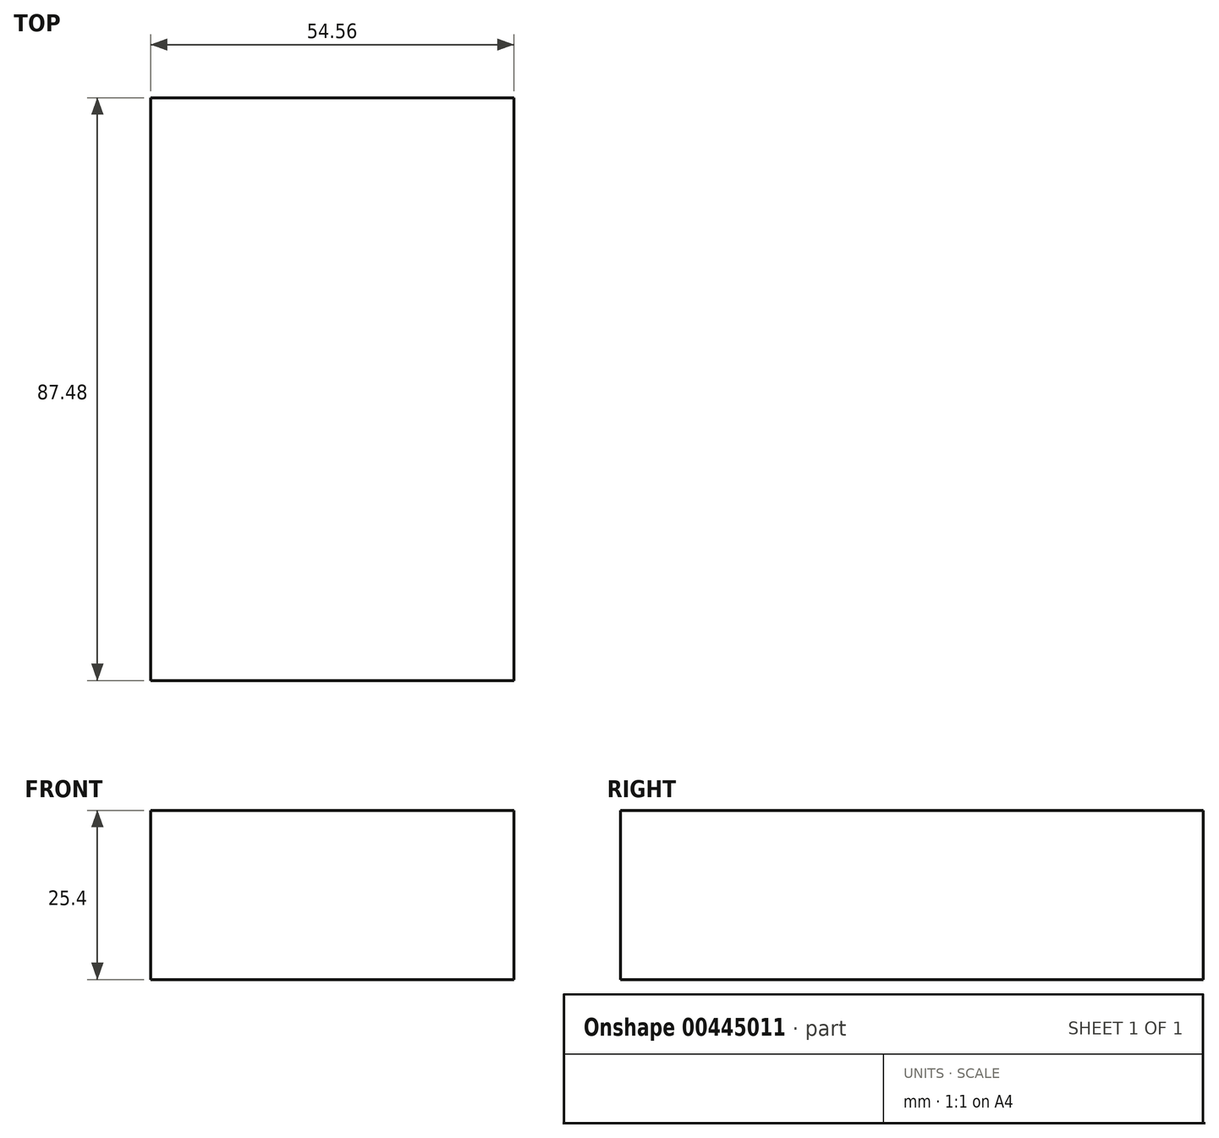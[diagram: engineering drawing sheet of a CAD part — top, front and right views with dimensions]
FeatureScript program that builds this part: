
annotation { "Feature Type Name" : "Feature", "Feature Type Description" : "" }
export const myFeature = defineFeature(function(context is Context, id is Id, definition is map)
    precondition{}
    {
        {
            var Q0;
            Q0=qCreatedBy(makeId("Top.planeOp"),FACE);
            var sketch = newSketch(context, id + "F0", { "sketchPlane" : qUnion([Q0])});
            skLineSegment(sketch, "E0.bottom", {"start": v(-23.9, -42.62) * mm, "end": v(30.65, -42.62) * mm});
            skLineSegment(sketch, "E0.top", {"start": v(-23.9, 44.86) * mm, "end": v(30.65, 44.86) * mm});
            skLineSegment(sketch, "E0.left", {"start": v(-23.9, -42.62) * mm, "end": v(-23.9, 44.86) * mm});
            skLineSegment(sketch, "E0.right", {"start": v(30.65, -42.62) * mm, "end": v(30.65, 44.86) * mm});
            skPoint(sketch, "E1", {"position": v(0, -23.11) * mm});
            skSolve(sketch);
        }
        {
            var Q0;
            Q0 = qSketchRegion(id + "F0", true);
            extrude(context, id + "F1", {"entities" : qUnion([Q0]), "depth" : 25.4 * mm});
        }
    });
